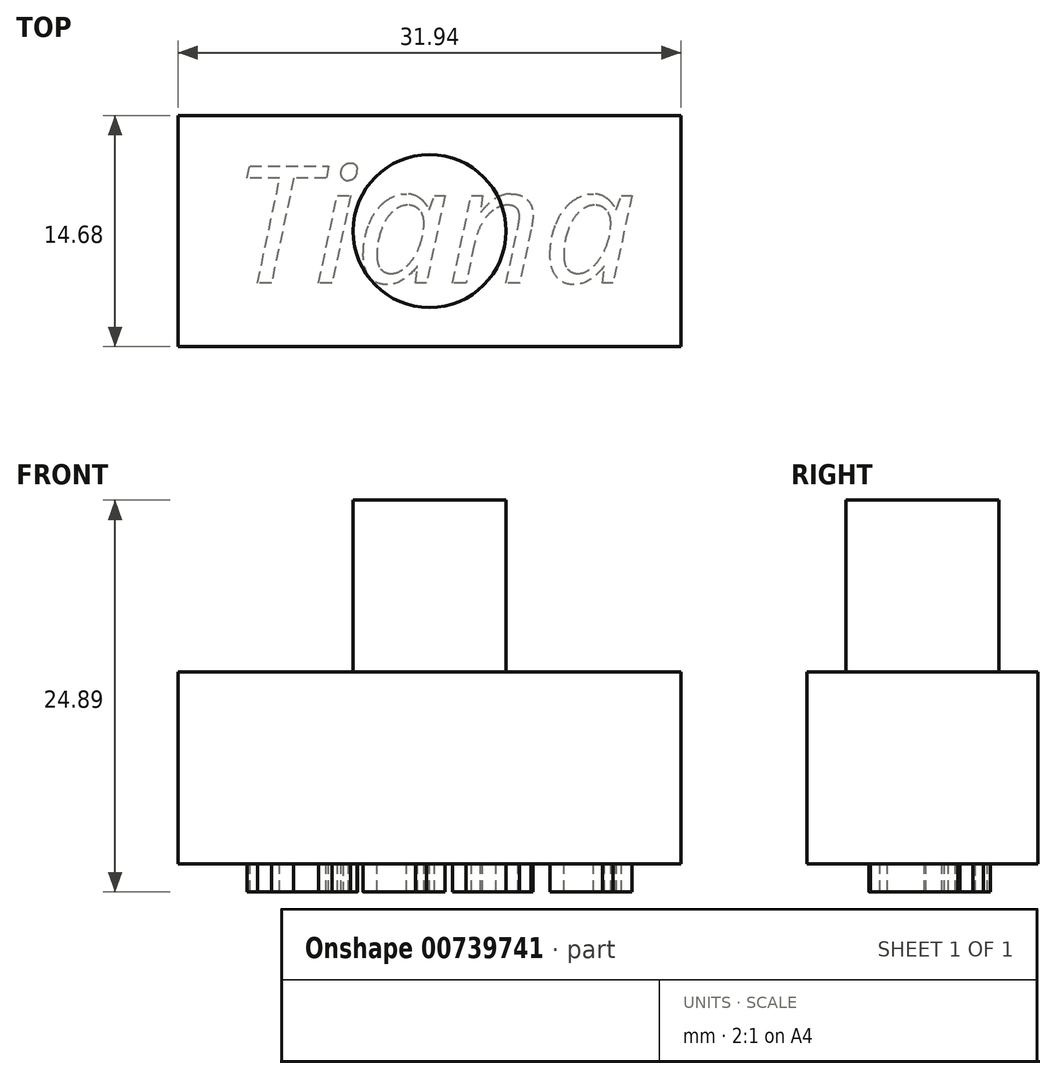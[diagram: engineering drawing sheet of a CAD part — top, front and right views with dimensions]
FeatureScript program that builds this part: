
annotation { "Feature Type Name" : "Feature", "Feature Type Description" : "" }
export const myFeature = defineFeature(function(context is Context, id is Id, definition is map)
    precondition{}
    {
        {
            var Q0;
            Q0=qCreatedBy(makeId("Top.planeOp"),FACE);
            var sketch = newSketch(context, id + "F0", { "sketchPlane" : qUnion([Q0])});
            skLineSegment(sketch, "E0.bottom", {"start": v(-15.97, -7.34) * mm, "end": v(15.97, -7.34) * mm});
            skLineSegment(sketch, "E0.top", {"start": v(-15.97, 7.34) * mm, "end": v(15.97, 7.34) * mm});
            skLineSegment(sketch, "E0.left", {"start": v(-15.97, -7.34) * mm, "end": v(-15.97, 7.34) * mm});
            skLineSegment(sketch, "E0.right", {"start": v(15.97, -7.34) * mm, "end": v(15.97, 7.34) * mm});
            skPoint(sketch, "E0.middle", {"position": v(0, 0) * mm});
            skSolve(sketch);
        }
        {
            var Q0;
            Q0 = qSketchRegion(id + "F0", true);
            extrude(context, id + "F1", {"entities" : qUnion([Q0]), "depth" : 12.2 * mm, "offsetDistance" : 25.4 * mm});
        }
        {
            var Q0;
            Q0=qCreatedBy(makeId("Top.planeOp"),FACE);
            var sketch = newSketch(context, id + "F2", { "sketchPlane" : qUnion([Q0])});
            skCircle(sketch, "E1", {"center": v(0, 0) * mm, "radius": 4.86 * mm});
            skSolve(sketch);
        }
        {
            var Q0;
            Q0 = qSketchRegion(id + "F2", true);
            extrude(context, id + "F3", {"entities" : qUnion([Q0]), "operationType" : NewBodyOperationType.ADD, "depth" : 23.1 * mm, "offsetDistance" : 25.4 * mm});
        }
        {
            var Q0;
            Q0=qCreatedBy(makeId("Top.planeOp"),FACE);
            var sketch = newSketch(context, id + "F4", { "sketchPlane" : qUnion([Q0])});
            skText(sketch, "E2", { "text": "Tiana", "fontName": "OpenSans-Italic.ttf"});
            const initialGuessF4  = {"E2": [-0.01252, -0.0033, 1, 0, 0.00748]};
            skSetInitialGuess(sketch, initialGuessF4);
            skSolve(sketch);
        }
        {
            var Q0;
            Q0 = qSketchRegion(id + "F4", true);
            extrude(context, id + "F5", {"entities" : qUnion([Q0]), "operationType" : NewBodyOperationType.ADD, "oppositeDirection" : true, "depth" : 1.78 * mm, "offsetDistance" : 25.4 * mm});
        }
    });
